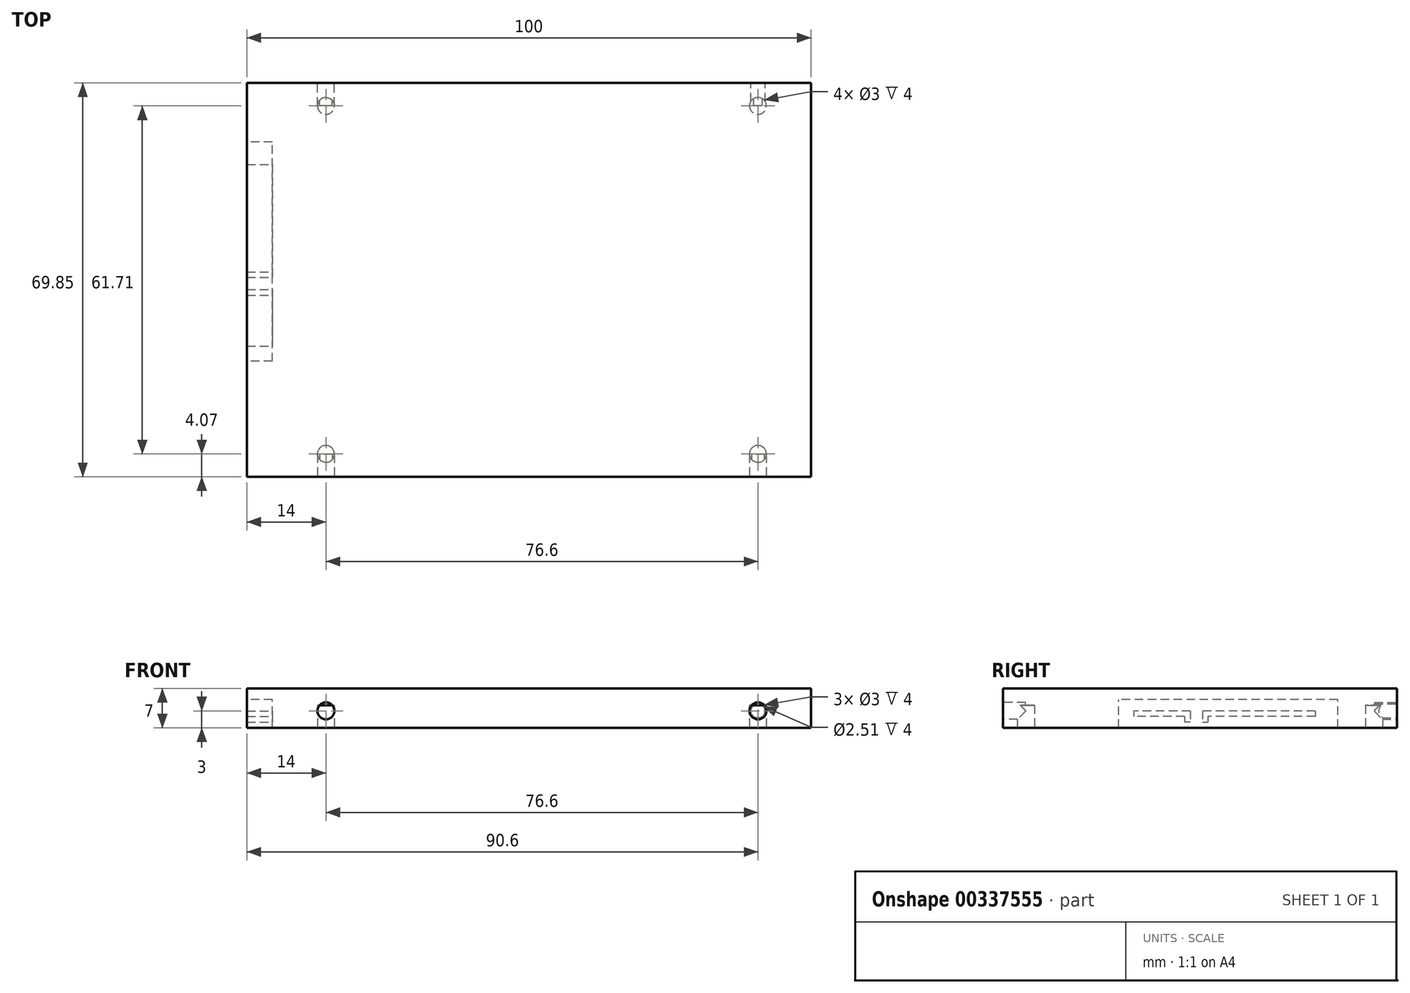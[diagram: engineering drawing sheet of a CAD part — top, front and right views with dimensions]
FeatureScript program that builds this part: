
annotation { "Feature Type Name" : "Feature", "Feature Type Description" : "" }
export const myFeature = defineFeature(function(context is Context, id is Id, definition is map)
    precondition{}
    {
        {
            var Q0;
            Q0=qCreatedBy(makeId("Top.planeOp"),FACE);
            var sketch = newSketch(context, id + "F0", { "sketchPlane" : qUnion([Q0])});
            skLineSegment(sketch, "E0.bottom", {"start": v(0, 0) * mm, "end": v(100, 0) * mm});
            skLineSegment(sketch, "E0.top", {"start": v(0, 69.85) * mm, "end": v(100, 69.85) * mm});
            skLineSegment(sketch, "E0.left", {"start": v(0, 0) * mm, "end": v(0, 69.85) * mm});
            skLineSegment(sketch, "E0.right", {"start": v(100, 0) * mm, "end": v(100, 69.85) * mm});
            skSolve(sketch);
        }
        {
            var Q0;
            Q0=qSketchRegion(id+"F0",true);
            extrude(context, id + "F1", {"entities" : qUnion([Q0]), "depth" : 7 * mm});
        }
        {
            var Q0;
            Q0=makeQuery(id+"F1.opExtrude","SWEPT_FACE",FACE,{"disambiguationData":[OSD([sQuery(id+"F0.wireOp",EDGE,"E0.left")])]});
            var sketch = newSketch(context, id + "F2", { "sketchPlane" : qUnion([Q0])});
            skLineSegment(sketch, "E1.bottom", {"start": v(-59.35, 0) * mm, "end": v(-20.5, 0) * mm});
            skLineSegment(sketch, "E1.top", {"start": v(-59.35, 5) * mm, "end": v(-20.5, 5) * mm});
            skLineSegment(sketch, "E1.left", {"start": v(-59.35, 0) * mm, "end": v(-59.35, 5) * mm});
            skLineSegment(sketch, "E1.right", {"start": v(-20.5, 0) * mm, "end": v(-20.5, 5) * mm});
            skSolve(sketch);
        }
        {
            var Q0;
            Q0=makeQuery(id+"F2.imprint","IMPRINT",FACE,{"disambiguationData":[TD([[makeQuery(id+"F2.imprint","IMPRINT",EDGE,{"derivedFrom":sQuery(id+"F2.wireOp",EDGE,"E1.bottom")}),-1.0]])]});
            extrude(context, id + "F3", {"entities" : qUnion([Q0]), "operationType" : NewBodyOperationType.REMOVE, "oppositeDirection" : true, "depth" : 4.5 * mm});
        }
        {
            var Q0;
            Q0=makeQuery(id+"F3.boolean.opBoolean","COPY",FACE,{"derivedFrom":makeQuery(id+"F3.opExtrude","CAP_FACE",FACE,{"disambiguationData":[OSD([sQuery(id+"F2.wireOp",EDGE,"E1.bottom"),sQuery(id+"F2.wireOp",EDGE,"E1.top"),sQuery(id+"F2.wireOp",EDGE,"E1.left"),sQuery(id+"F2.wireOp",EDGE,"E1.right")])],"isStart":false})});
            var sketch = newSketch(context, id + "F4", { "sketchPlane" : qUnion([Q0])});
            skLineSegment(sketch, "E2.bottom", {"start": v(-55.35, 3) * mm, "end": v(-35.35, 3) * mm});
            skLineSegment(sketch, "E2.top", {"start": v(-55.35, 2) * mm, "end": v(-36.35, 2) * mm});
            skLineSegment(sketch, "E2.left", {"start": v(-55.35, 3) * mm, "end": v(-55.35, 2) * mm});
            skLineSegment(sketch, "E2.right", {"start": v(-35.35, 3) * mm, "end": v(-35.35, 2) * mm});
            skLineSegment(sketch, "E3.top", {"start": v(-35.35, 1) * mm, "end": v(-36.35, 1) * mm});
            skLineSegment(sketch, "E3.left", {"start": v(-35.35, 2) * mm, "end": v(-35.35, 1) * mm});
            skLineSegment(sketch, "E3.right", {"start": v(-36.35, 2) * mm, "end": v(-36.35, 1) * mm});
            skLineSegment(sketch, "E4.bottom", {"start": v(-33.2, 3) * mm, "end": v(-23.2, 3) * mm});
            skLineSegment(sketch, "E4.top", {"start": v(-33.2, 2) * mm, "end": v(-23.2, 2) * mm});
            skLineSegment(sketch, "E4.left", {"start": v(-33.2, 3) * mm, "end": v(-33.2, 2) * mm});
            skLineSegment(sketch, "E4.right", {"start": v(-23.2, 3) * mm, "end": v(-23.2, 2) * mm});
            skLineSegment(sketch, "E5.bottom", {"start": v(-33.2, 2) * mm, "end": v(-32.2, 2) * mm});
            skLineSegment(sketch, "E5.top", {"start": v(-33.2, 1) * mm, "end": v(-32.2, 1) * mm});
            skLineSegment(sketch, "E5.left", {"start": v(-33.2, 2) * mm, "end": v(-33.2, 1) * mm});
            skLineSegment(sketch, "E5.right", {"start": v(-32.2, 2) * mm, "end": v(-32.2, 1) * mm});
            skLineSegment(sketch, "E6", {"start": v(-35.35, 3) * mm, "end": v(-33.2, 3) * mm, "construction": true});
            skLineSegment(sketch, "E7", {"start": v(-35.35, 2) * mm, "end": v(-33.2, 2) * mm, "construction": true});
            skLineSegment(sketch, "E8", {"start": v(-35.35, 1) * mm, "end": v(-33.2, 1) * mm, "construction": true});
            skSolve(sketch);
        }
        {
            var Q0;
            Q0=qSketchRegion(id+"F4",true);
            extrude(context, id + "F5", {"entities" : qUnion([Q0]), "operationType" : NewBodyOperationType.ADD, "depth" : 4.5 * mm});
        }
        {
            var Q0;
            Q0=makeQuery(id+"F1.opExtrude","CAP_FACE",FACE,{"disambiguationData":[OSD([sQuery(id+"F0.wireOp",EDGE,"E0.bottom"),sQuery(id+"F0.wireOp",EDGE,"E0.top"),sQuery(id+"F0.wireOp",EDGE,"E0.left"),sQuery(id+"F0.wireOp",EDGE,"E0.right")])],"isStart":true});
            var sketch = newSketch(context, id + "F6", { "sketchPlane" : qUnion([Q0])});
            skCircle(sketch, "E9", {"center": v(14, -65.78) * mm, "radius": 1.5 * mm});
            skCircle(sketch, "E10", {"center": v(14, -4.07) * mm, "radius": 1.5 * mm});
            skCircle(sketch, "E11", {"center": v(90.6, -65.78) * mm, "radius": 1.5 * mm});
            skCircle(sketch, "E12", {"center": v(90.6, -4.07) * mm, "radius": 1.5 * mm});
            skLineSegment(sketch, "E13", {"start": v(14, -65.78) * mm, "end": v(90.6, -65.78) * mm, "construction": true});
            skLineSegment(sketch, "E14", {"start": v(14, -65.78) * mm, "end": v(14, -4.07) * mm, "construction": true});
            skLineSegment(sketch, "E15", {"start": v(90.6, -4.07) * mm, "end": v(14, -4.07) * mm, "construction": true});
            skLineSegment(sketch, "E16", {"start": v(90.6, -4.07) * mm, "end": v(90.6, -65.78) * mm, "construction": true});
            skSolve(sketch);
        }
        {
            var Q0;
            Q0=qSketchRegion(id+"F6",true);
            extrude(context, id + "F7", {"entities" : qUnion([Q0]), "operationType" : NewBodyOperationType.REMOVE, "oppositeDirection" : true, "depth" : 4 * mm});
        }
        {
            var Q0;
            Q0=makeQuery(id+"F1.opExtrude","SWEPT_FACE",FACE,{"disambiguationData":[OSD([sQuery(id+"F0.wireOp",EDGE,"E0.top")])]});
            var sketch = newSketch(context, id + "F8", { "sketchPlane" : qUnion([Q0])});
            skCircle(sketch, "E17", {"center": v(-14, 3) * mm, "radius": 1.5 * mm});
            skCircle(sketch, "E18", {"center": v(-90.6, 3) * mm, "radius": 1.26 * mm});
            skLineSegment(sketch, "E19", {"start": v(-14, 3) * mm, "end": v(-90.6, 3) * mm, "construction": true});
            skSolve(sketch);
        }
        {
            var Q0;
            Q0=qSketchRegion(id+"F8",true);
            extrude(context, id + "F9", {"entities" : qUnion([Q0]), "operationType" : NewBodyOperationType.REMOVE, "oppositeDirection" : true, "depth" : 4 * mm});
        }
        {
            var Q0;
            Q0=makeQuery(id+"F1.opExtrude","SWEPT_FACE",FACE,{"disambiguationData":[OSD([sQuery(id+"F0.wireOp",EDGE,"E0.bottom")])]});
            var sketch = newSketch(context, id + "F10", { "sketchPlane" : qUnion([Q0])});
            skCircle(sketch, "E20", {"center": v(90.6, 3) * mm, "radius": 1.5 * mm});
            skCircle(sketch, "E21", {"center": v(14, 3) * mm, "radius": 1.5 * mm});
            skLineSegment(sketch, "E22", {"start": v(90.6, 3) * mm, "end": v(14, 3) * mm, "construction": true});
            skSolve(sketch);
        }
        {
            var Q0;
            Q0=qSketchRegion(id+"F10",true);
            extrude(context, id + "F11", {"entities" : qUnion([Q0]), "operationType" : NewBodyOperationType.REMOVE, "oppositeDirection" : true, "depth" : 4 * mm});
        }
    });
